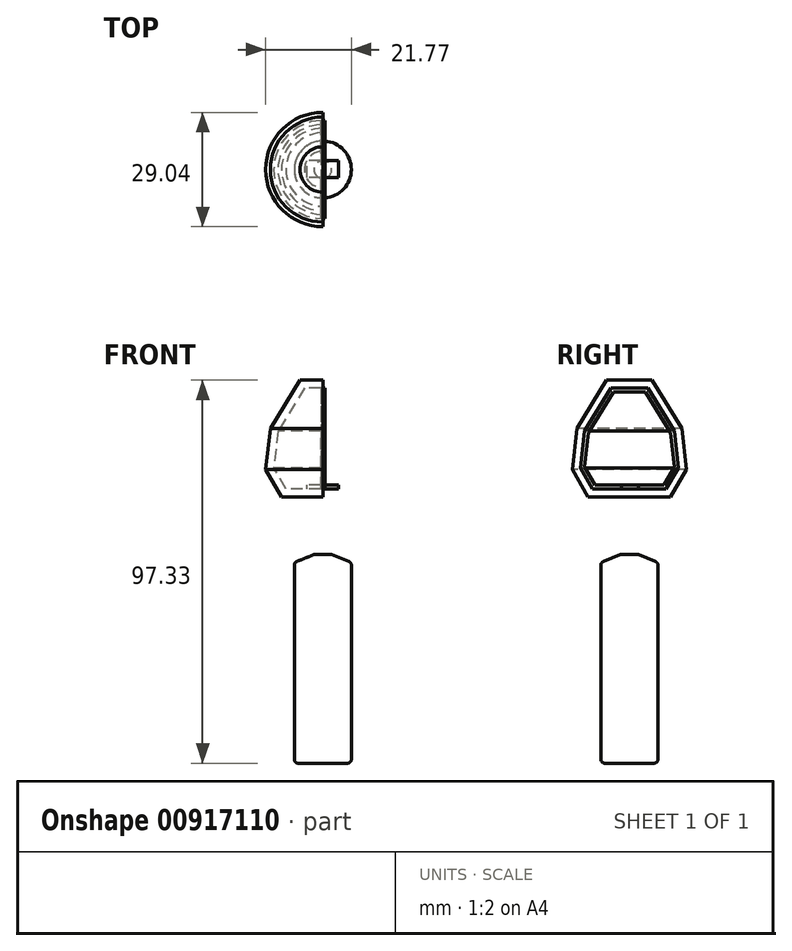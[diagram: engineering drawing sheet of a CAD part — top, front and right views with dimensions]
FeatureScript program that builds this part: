
annotation { "Feature Type Name" : "Feature", "Feature Type Description" : "" }
export const myFeature = defineFeature(function(context is Context, id is Id, definition is map)
    precondition{}
    {
        {
            var Q0;
            Q0=qCreatedBy(makeId("Front.planeOp"),FACE);
            var sketch = newSketch(context, id + "F0", { "sketchPlane" : qUnion([Q0])});
            skLineSegment(sketch, "E0.bottom", {"start": v(0, -23.42) * mm, "end": v(-7.25, -23.42) * mm});
            skLineSegment(sketch, "E0.top", {"start": v(0, 29.58) * mm, "end": v(-7.25, 29.58) * mm});
            skLineSegment(sketch, "E0.left", {"start": v(0, -23.42) * mm, "end": v(0, 29.58) * mm});
            skLineSegment(sketch, "E0.right", {"start": v(-7.25, -23.42) * mm, "end": v(-7.25, 29.58) * mm});
            skSolve(sketch);
        }
        {
            var Q0;
            Q0=makeQuery(id+"F0.imprint","IMPRINT",FACE,{"disambiguationData":[TD([[makeQuery(id+"F0.imprint","IMPRINT",EDGE,{"derivedFrom":sQuery(id+"F0.wireOp",EDGE,"E0.bottom")}),-1.0]])]});
            var Q1;
            Q1=sQuery(id+"F0.wireOp",EDGE,"E0.left");
            revolve(context, id + "F1", {"surfaceOperationType" : NewSurfaceOperationType.NEW, "entities" : qUnion([Q0]), "axis" : qUnion([Q1]), "revolveType" : RevolveType.FULL});
        }
        {
            var Q0;
            Q0=makeQuery(id+"F1.opRevolve","SWEPT_EDGE",EDGE,{"disambiguationData":[OSD([sQuery(id+"F0.wireOp",EDGE,"E0.top"),sQuery(id+"F0.wireOp",EDGE,"E0.right")])]});
            chamfer(context, id + "F2", {"entities" : qUnion([Q0]), "chamferType" : ChamferType.TWO_OFFSETS, "width1" : 2 * mm, "oppositeDirection" : false, "width2" : 5 * mm, "tangentPropagation" : true});
        }
        {
            var Q0;
            {var subQ0=sQuery(id+"F0.wireOp",EDGE,"E0.right");Q0=makeQuery(id+"F2.opChamfer","BLEND_EDGE",EDGE,{"blendedFrom":[makeQuery(id+"F1.opRevolve","SWEPT_EDGE",EDGE,{"disambiguationData":[OSD([sQuery(id+"F0.wireOp",EDGE,"E0.top"),subQ0])]}),makeQuery(id+"F1.opRevolve","SWEPT_FACE",FACE,{"disambiguationData":[OSD([subQ0])]})],"blendedInto":[makeQuery(id+"F1.opRevolve","SWEPT_FACE",FACE,{"disambiguationData":[OSD([subQ0])]})]});}
            var Q1;
            Q1=makeQuery(id+"F1.opRevolve","SWEPT_EDGE",EDGE,{"disambiguationData":[OSD([sQuery(id+"F0.wireOp",EDGE,"E0.bottom"),sQuery(id+"F0.wireOp",EDGE,"E0.right")])]});
            fillet(context, id + "F3", {"entities" : qUnion([Q0, Q1]), "radius" : 1 * mm, "tangentPropagation" : true, "allowEdgeOverflow" : false});
        }
        {
            var Q0;
            Q0=qCreatedBy(makeId("Right.planeOp"),FACE);
            var sketch = newSketch(context, id + "F4", { "sketchPlane" : qUnion([Q0])});
            skLineSegment(sketch, "E1", {"start": v(0, 71.9) * mm, "end": v(-4.65, 71.9) * mm});
            skLineSegment(sketch, "E2", {"start": v(-4.65, 71.9) * mm, "end": v(-11.4, 60.97) * mm});
            skLineSegment(sketch, "E3", {"start": v(-11.4, 60.97) * mm, "end": v(-12.46, 51.65) * mm});
            skLineSegment(sketch, "E4", {"start": v(-12.46, 51.65) * mm, "end": v(-9.34, 46.28) * mm});
            skLineSegment(sketch, "E5", {"start": v(-9.34, 46.28) * mm, "end": v(0, 46.28) * mm});
            skLineSegment(sketch, "E6.0", {"start": v(-10.49, 44.28) * mm, "end": v(0, 44.28) * mm});
            skLineSegment(sketch, "E6.1", {"start": v(0, 73.9) * mm, "end": v(-5.77, 73.9) * mm});
            skLineSegment(sketch, "E6.2", {"start": v(-5.77, 73.9) * mm, "end": v(-13.33, 61.64) * mm});
            skLineSegment(sketch, "E6.3", {"start": v(-13.33, 61.64) * mm, "end": v(-14.52, 51.21) * mm});
            skLineSegment(sketch, "E6.4", {"start": v(-14.52, 51.21) * mm, "end": v(-10.49, 44.28) * mm});
            skLineSegment(sketch, "E7", {"start": v(0, 73.9) * mm, "end": v(0, 71.9) * mm});
            skLineSegment(sketch, "E8", {"start": v(0, 46.28) * mm, "end": v(0, 44.28) * mm});
            skLineSegment(sketch, "E9.0", {"start": v(-8.76, 47.28) * mm, "end": v(0, 47.28) * mm});
            skLineSegment(sketch, "E9.1", {"start": v(0, 70.9) * mm, "end": v(-4.1, 70.9) * mm});
            skLineSegment(sketch, "E9.2", {"start": v(-4.1, 70.9) * mm, "end": v(-10.43, 60.63) * mm});
            skLineSegment(sketch, "E9.3", {"start": v(-10.43, 60.63) * mm, "end": v(-11.43, 51.86) * mm});
            skLineSegment(sketch, "E9.4", {"start": v(-11.43, 51.86) * mm, "end": v(-8.76, 47.28) * mm});
            skLineSegment(sketch, "E10", {"start": v(0, 70.9) * mm, "end": v(0, 71.9) * mm});
            skLineSegment(sketch, "E11", {"start": v(0, 47.28) * mm, "end": v(0, 46.28) * mm});
            skLineSegment(sketch, "E12.MirrorCS", {"start": v(0, 70.9) * mm, "end": v(4.1, 70.9) * mm});
            skLineSegment(sketch, "E13.MirrorCS", {"start": v(0, 71.9) * mm, "end": v(4.65, 71.9) * mm});
            skLineSegment(sketch, "E14.MirrorCS", {"start": v(4.65, 71.9) * mm, "end": v(11.4, 60.97) * mm});
            skLineSegment(sketch, "E15.MirrorCS", {"start": v(4.1, 70.9) * mm, "end": v(10.43, 60.63) * mm});
            skLineSegment(sketch, "E16.MirrorCS", {"start": v(11.4, 60.97) * mm, "end": v(12.46, 51.65) * mm});
            skLineSegment(sketch, "E17.MirrorCS", {"start": v(10.43, 60.63) * mm, "end": v(11.43, 51.86) * mm});
            skLineSegment(sketch, "E18.MirrorCS", {"start": v(12.46, 51.65) * mm, "end": v(9.34, 46.28) * mm});
            skLineSegment(sketch, "E19.MirrorCS", {"start": v(11.43, 51.86) * mm, "end": v(8.76, 47.28) * mm});
            skLineSegment(sketch, "E20.MirrorCS", {"start": v(8.76, 47.28) * mm, "end": v(0, 47.28) * mm});
            skLineSegment(sketch, "E21.MirrorCS", {"start": v(9.34, 46.28) * mm, "end": v(0, 46.28) * mm});
            skLineSegment(sketch, "E22", {"start": v(-2.07, 47.28) * mm, "end": v(-2.07, 46.28) * mm});
            skLineSegment(sketch, "E23", {"start": v(-2.07, 46.28) * mm, "end": v(2.33, 46.28) * mm});
            skLineSegment(sketch, "E24", {"start": v(2.33, 46.28) * mm, "end": v(2.33, 47.28) * mm});
            skSolve(sketch);
        }
        {
            var Q0;
            Q0=makeQuery(id+"F4.imprint","IMPRINT",FACE,{"disambiguationData":[TD([[makeQuery(id+"F4.imprint","IMPRINT",EDGE,{"derivedFrom":sQuery(id+"F4.wireOp",EDGE,"E1")}),-1.0]])]});
            var Q1;
            Q1=sQuery(id+"F4.wireOp",EDGE,"E7");
            revolve(context, id + "F5", {"surfaceOperationType" : NewSurfaceOperationType.NEW, "entities" : qUnion([Q0]), "axis" : qUnion([Q1]), "revolveType" : RevolveType.ONE_DIRECTION, "angle" : 180 * degree});
        }
        {
            var Q0;
            Q0=makeQuery(id+"F4.imprint","IMPRINT",FACE,{"disambiguationData":[TD([[makeQuery(id+"F4.imprint","IMPRINT",EDGE,{"derivedFrom":sQuery(id+"F4.wireOp",EDGE,"E1")}),1.0]])]});
            var Q1;
            Q1=makeQuery(id+"F4.imprint","IMPRINT",FACE,{"disambiguationData":[TD([[makeQuery(id+"F4.imprint","IMPRINT",EDGE,{"derivedFrom":sQuery(id+"F4.wireOp",EDGE,"E10")}),-1.0]])]});
            extrude(context, id + "F6", {"entities" : qUnion([Q0, Q1]), "operationType" : NewBodyOperationType.ADD, "endBound" : BoundingType.SYMMETRIC, "depth" : 1 * mm, "offsetDistance" : 25 * mm});
        }
        {
            var Q0;
            {var subQ0=sQuery(id+"F4.wireOp",EDGE,"E11");Q0=makeQuery(id+"F4.imprint","IMPRINT",FACE,{"disambiguationData":[TD([[makeQuery(id+"F4.imprint","IMPRINT",EDGE,{"derivedFrom":subQ0}),-1.0]])]});}
            var Q1;
            {var subQ0=sQuery(id+"F4.wireOp",EDGE,"E11");Q1=makeQuery(id+"F4.imprint","IMPRINT",FACE,{"disambiguationData":[TD([[makeQuery(id+"F4.imprint","IMPRINT",EDGE,{"derivedFrom":subQ0}),1.0]])]});}
            extrude(context, id + "F7", {"entities" : qUnion([Q0, Q1]), "operationType" : NewBodyOperationType.ADD, "endBound" : BoundingType.SYMMETRIC, "depth" : 8 * mm, "offsetDistance" : 25 * mm});
        }
    });
